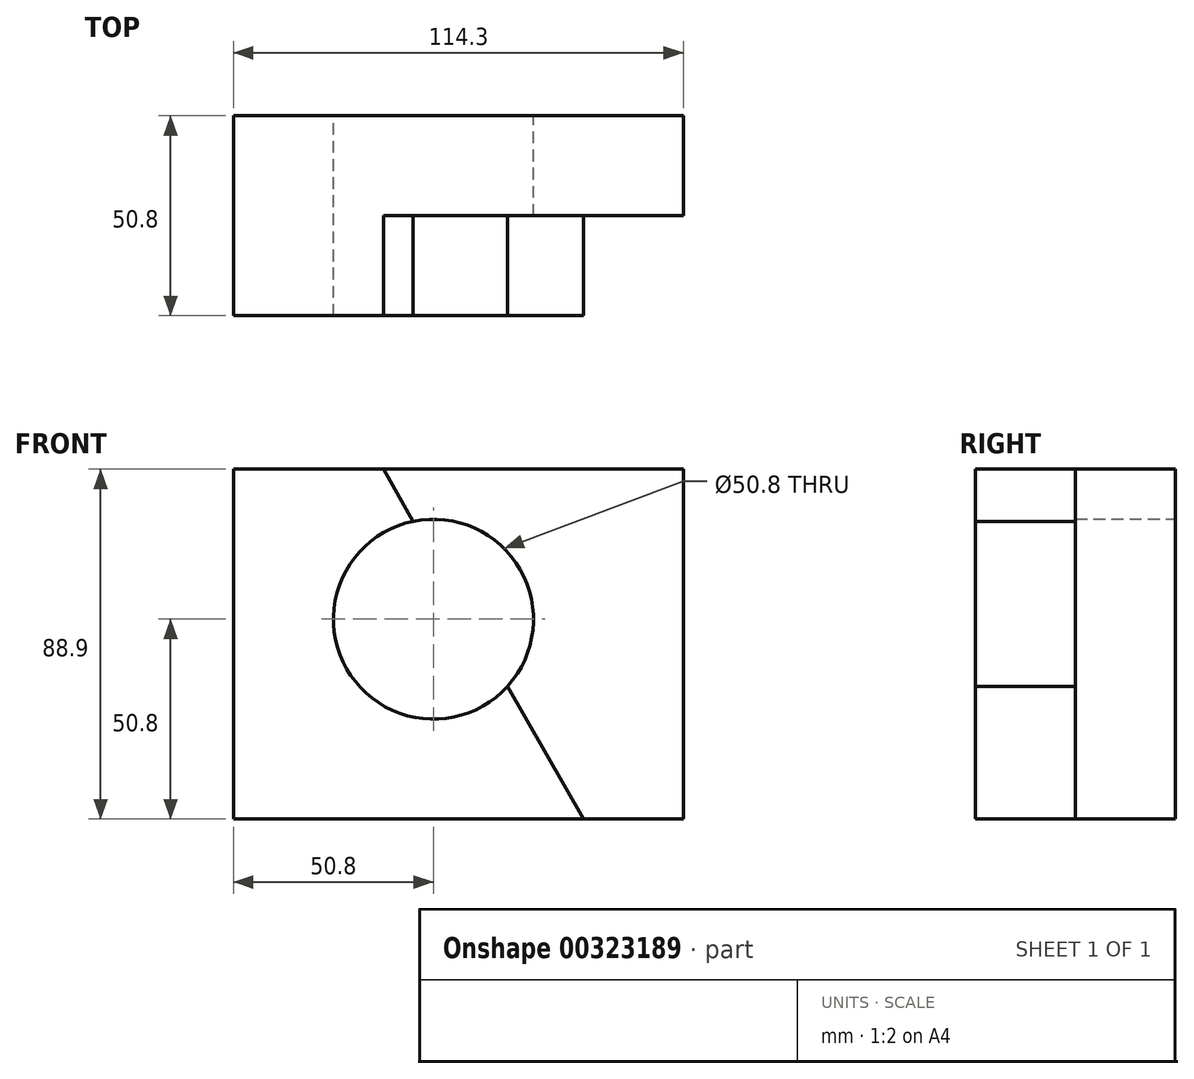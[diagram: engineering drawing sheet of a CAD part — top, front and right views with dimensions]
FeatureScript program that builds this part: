
annotation { "Feature Type Name" : "Feature", "Feature Type Description" : "" }
export const myFeature = defineFeature(function(context is Context, id is Id, definition is map)
    precondition{}
    {
        {
            var Q0;
            Q0=qCreatedBy(makeId("Front.planeOp"),FACE);
            var sketch = newSketch(context, id + "F0", { "sketchPlane" : qUnion([Q0])});
            skLineSegment(sketch, "E0.bottom", {"start": v(57.15, 44.45) * mm, "end": v(-57.15, 44.45) * mm});
            skLineSegment(sketch, "E0.top", {"start": v(57.15, -44.45) * mm, "end": v(-57.15, -44.45) * mm});
            skLineSegment(sketch, "E0.left", {"start": v(57.15, 44.45) * mm, "end": v(57.15, -44.45) * mm});
            skLineSegment(sketch, "E0.right", {"start": v(-57.15, 44.45) * mm, "end": v(-57.15, -44.45) * mm});
            skLineSegment(sketch, "E1", {"start": v(-19.05, 44.45) * mm, "end": v(31.75, -44.45) * mm});
            skCircle(sketch, "E2", {"center": v(-6.35, 6.35) * mm, "radius": 25.4 * mm});
            skSolve(sketch);
        }
        {
            var Q0;
            {var subQ5=sQuery(id+"F0.wireOp",EDGE,"E0.left");Q0=makeQuery(id+"F0.imprint","IMPRINT",FACE,{"disambiguationData":[TD([[makeQuery(id+"F0.imprint","IMPRINT",EDGE,{"derivedFrom":subQ5}),-1.0]])]});}
            extrude(context, id + "F1", {"entities" : qUnion([Q0]), "depth" : 25.4 * mm});
        }
        {
            var Q0;
            {var subQ0=sQuery(id+"F0.wireOp",EDGE,"E0.right");Q0=makeQuery(id+"F0.imprint","IMPRINT",FACE,{"disambiguationData":[TD([[makeQuery(id+"F0.imprint","IMPRINT",EDGE,{"derivedFrom":subQ0}),1.0]])]});}
            extrude(context, id + "F2", {"entities" : qUnion([Q0]), "operationType" : NewBodyOperationType.ADD, "depth" : 50.8 * mm});
        }
    });
